# Revit family: Vexo_PipeAccessories_XPot61
name_source: partatom
category: Pipe Accessories
revit_build: Autodesk Revit 2018 (Build: 20190510_1515(x64)
units: mm (PartAtom-declared; Revit-internal decimal feet)

## family parameters
Always vertical = No
Cut with Voids When Loaded = Yes
OmniClass Number = 23.60.10.11
OmniClass Title = Temperature Measuring Instruments
Part Type = Sensor
Round Connector Dimension = Use Diameter
Shared = No
Work Plane-Based = Yes

## types (1)
- XPOT 6
    10L Dosing Pot Capacity = Enables installers and maintenance personnel to quickly dose the system
with water treatment chemicals.
    6No 8,500 Gauss Neodymium Magnets = Each magnet is fully encased in 304SS shell, easily removable from the
316SS Magnet Grate for cleaning and fully submerged in the system flow
for increased filtration.
    Application = Side Stream Filtration & Dosing Unit
    Assembly Code = D20
    AssetIdentifier (default) = Please record on commissioning
    AssetType = Fixed
    Automatic Air Separator = Ensures the system micro-bubbles and air are emitted from the system
and helps to reduce corrosion rates and decreases stress on system
components.
    Automatic Air Vent = Brass
    BIMObjectName = Vexo_PipeAccessories_XPot6
    Baffle Plate = 316 Stainless Steel
    BarCode (default) = Please record on commissioning
    Bespoke Insulation Jacket = Supplied as part of the Starter Pack. The bespoke insulation jacket ensures
heat losses are minimised.
    CE / EMC Compatibility = IEC 61010-1: 2010 + A1: 2019 and EN 61010-1: 2010 + A1:2019
    Cartridge Filter = Polypropylene Spun Bonded Fibre
    ClassificationName = Uniclass2015
    ClassificationValue = Pr_75_51_17_78
    Color = Grey & Green
    Compliance = Fully compliant with BSRIA Guidelines BG29 and BG50 for Chemical
Dosing, Magnetic Filtration, Fine Filtration, Passive Deaeration and Side
Stream Filtration.
    Connections 1” BSP = Suitable for all types of closed loop LTHW Heating and Cooling Water
Systems up to 86,400Litres in volume.
    Default Elevation = 1200 mm
    Description = X-Pot 6 Side Stream Filter              ﻿     ﻿     ​         ​              ﻿                           ​﻿﻿
    DocumentationCertificates = http://www.vexoint.com
    DocumentationInstallationGuide = https://www.bimstore.co
    DocumentationMaintenance = http://www.vexoint.com
    DocumentationTechnical = https://www.bimstore.co
    Dosing Capacity = 10L
    Enhanced Performance = The ingenious design ensures that the filter will continue to perform should regular maintenance not be carried out.
filter will not inhibit system performance.
    Filter Body Mounting = Wall or Floor Standing (Unistrut)
    Filtration Rate = Down to 0.5 Micron
    Finish = Stainless Steel
    Fittings = 304 Stainless Steel
    Full Bore Ball Valve isolation Valves = The 304SS isolation valves do not restrict system flow and increases ease
of installation.
    General Description = Side stream filtration including
magnet filter, cartridge filter,
air and dirt separator
and dosing unit for medium to
large commercial systems.
    HandedLeft = No
    HandedRight = Yes
    Installation Bracket = Complete with backing plate for simple installation to wall or frame.
    InstallationDate (default) = Please record on commissioning
    Isolation Valve Connections = 1” BSP Female
    Isolation Valves = 304 Stainless Steel
    Keynote = ﻿﻿​S        ﻿﻿  ﻿ ﻿   ﻿ ﻿ ﻿     ﻿   ﻿ ﻿   ﻿ ﻿     ​                      ﻿     ﻿     ​         ​              ﻿                           ​﻿﻿
    Magnet Grate = 316 Stainless Steel
    Magnetic Filter = Removes magnetic system debris, increases the lifespan of the boiler,
chiller and cooling system components, reduces carbon emissions,
increases fuel efficiency and increases the lifespan of the Cartridge Filter.
    Magnets = Neodymium Rare Earth
    Manufacturer = Vexo Int
    ManufacturerName = Vexo Int
    Material = 304 Stainless Steel
    Max Flow Rate = 60L/min
    Max System Volume = 86400 Litres
    Max Working Pressure = 7Bar
    Max Working Temperature = 95oC
    Min Flow Rate = 4.98L/min
    Min Working Temperature = 0oC
    Model = X-Pot 6 Side Stream Filter
    ModelNumber = X-Pot 6 Side Stream Filter
    ModelReference = X-Pot 6 Side Stream Filter                         ﻿     ﻿     ​         ​              ﻿                           ​﻿﻿
    NBSDescription = Side Stream Filtration & Dosing Unit
Side Stream Filtration & Dosing Unit
Side Stream Filtration & Dosing Unit
    NBSObjectName = Vexo Products - Side Stream Filtration & Dosing Unit
    NominalDepth = 305 mm
    NominalHeight = 915 mm
    NominalLength = 460 mm
    NominalWidth = 460 mm
    Non Return Valve = 304 Stainless Steel
    OutPutPosition = 285 mm
    Polypropylene Cartridge Filter = Removes non-magnetic system debris, available in 50, 20, 5 & 0.5
micron filtration rates, ensures coalescence micro-bubble formation on the
surface of the filter & surpasses BSRIA Guidance for filtration rates.
    Product Code = VX-XPOTXPOT6
    ProductionYear = 2020
    SerialNumber (default) = Please record on commissioning
    Servicing = The cleaning of the filters can simply be achieved without the need to
shut the main system down and the dosing of water treatment chemicals
is achieved simply and safely, again without the need to shut the system
down.
    Shape = Cylindrical
    Stainless Steel Components = All major components are manufactured from 304SS or 316SS for
improved lifecycle and reliability.
    Starter Pack Product Code = V-XPOT6(CONT)PACK
    Type Comments = X-Pot 6 Side Stream Filter                         ﻿     ﻿     ​         ​              ﻿                           ​﻿﻿
    TypeName = X-Pot 6 Side Stream Filter                         ﻿     ﻿     ​         ​              ﻿                           ​﻿﻿
    URL = http://www.vexoint.com
    Vessel Body = 304 Stainless Steel – complies with PED 2014/68/EU SEP
    WarrantyDescription = 5 Years Standard (6 Years if VEXOTM X-PO10 Inhibitor is used)
    WarrantyStartDate (default) = Please record on commissioning
    Weight (Empty) = 21kg
    Weight (Full) = 34kg
    X-PO10 Inhibitor 10L = VX-XPO10-10LTR
    X-PO20 De-Scaler  10L = VX-XPO20-10LTR
    X-PO35 Non-Flush Cleanser 10L = VX-XPO35-10LTR
    X-PO40 De-Sludger 10L = VX-XPO40-10LTR
    X-PO45 New System 10L = VX-XPO45-10LTR
    X-PO50 Anti-Freeze 20L = VX-XPO50-20LTR
    X-PO55 Anti-Freeze 20L = VX-XPO55-20LTR
    X-PO80 Biocide 5L = VX-XPO80-5LTR
    _BSBibleVersion = 16
    _BimSpecGuid = 0
    _CurrentRevision = 2
    _DistributedBy = Vexo Int

## geometry (parser evidence)
native form markers: Blend x4, Sweep x3
no freeform markers — native parametric forms only
